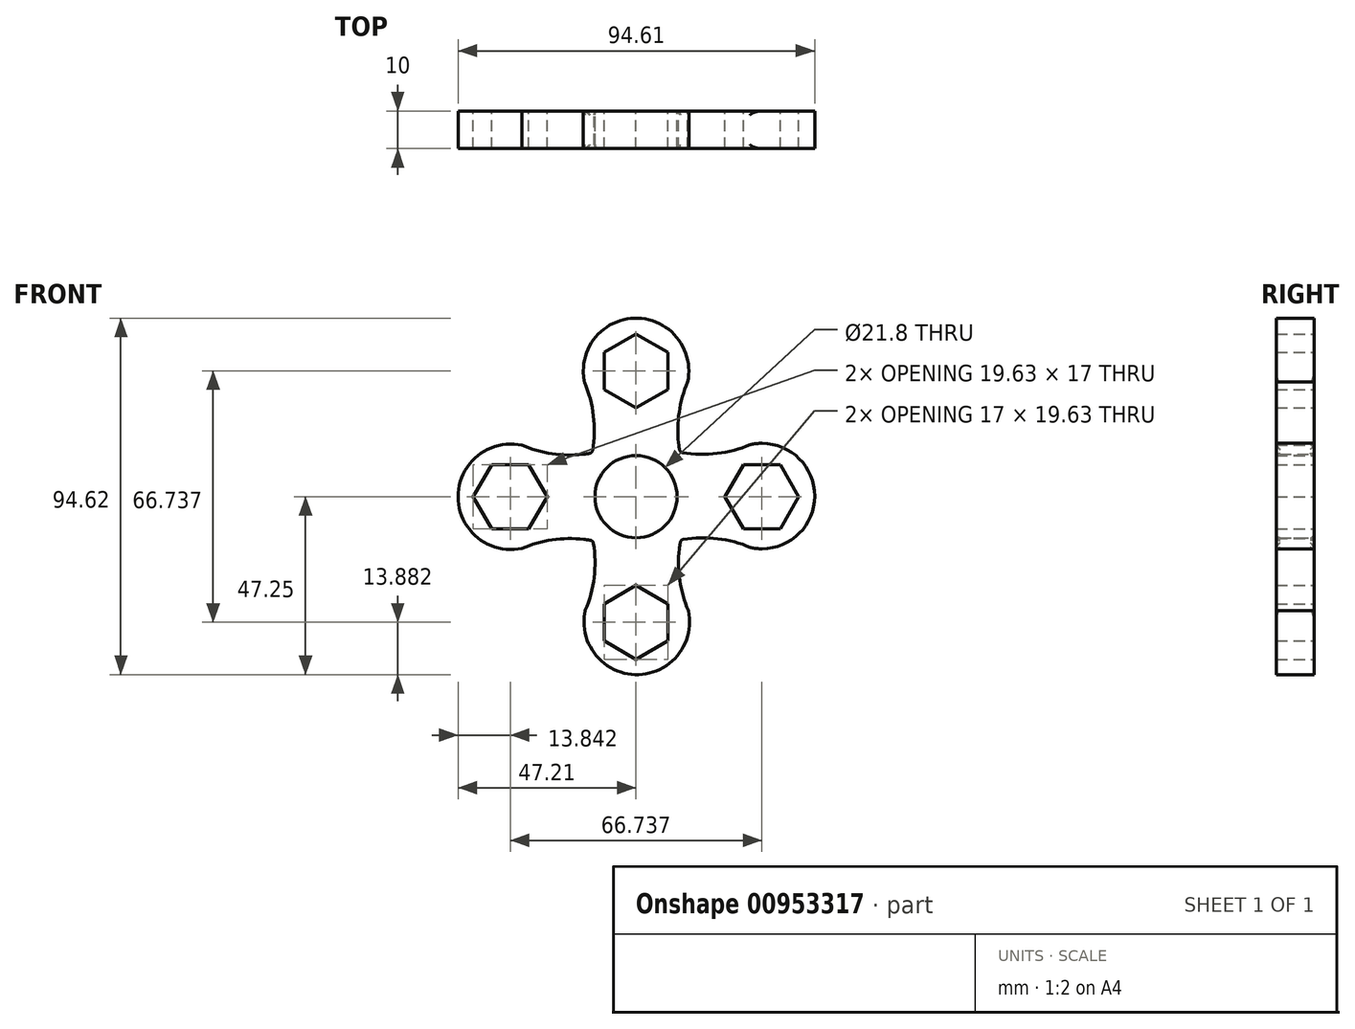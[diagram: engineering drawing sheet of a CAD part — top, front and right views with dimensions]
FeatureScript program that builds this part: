
annotation { "Feature Type Name" : "Feature", "Feature Type Description" : "" }
export const myFeature = defineFeature(function(context is Context, id is Id, definition is map)
    precondition{}
    {
        {
            var Q0;
            Q0=qCreatedBy(makeId("Front.planeOp"),FACE);
            var sketch = newSketch(context, id + "F0", { "sketchPlane" : qUnion([Q0])});
            skCircle(sketch, "E0", {"center": v(0, 0) * mm, "radius": 10.9 * mm});
            skCircle(sketch, "E1.cCircle", {"center": v(0, 33.37) * mm, "radius": 8.5 * mm, "construction": true});
            skLineSegment(sketch, "E1.0", {"start": v(8.5, 38.28) * mm, "end": v(8.5, 28.46) * mm});
            skLineSegment(sketch, "E1.1", {"start": v(8.5, 28.46) * mm, "end": v(0, 23.55) * mm});
            skLineSegment(sketch, "E1.2", {"start": v(0, 23.55) * mm, "end": v(-8.5, 28.46) * mm});
            skLineSegment(sketch, "E1.3", {"start": v(-8.5, 28.46) * mm, "end": v(-8.5, 38.28) * mm});
            skLineSegment(sketch, "E1.4", {"start": v(-8.5, 38.28) * mm, "end": v(0, 43.18) * mm});
            skLineSegment(sketch, "E1.5", {"start": v(0, 43.18) * mm, "end": v(8.5, 38.28) * mm});
            skPoint(sketch, "E1.0.midPoint", {"position": v(8.5, 33.37) * mm});
            skCircle(sketch, "E2.1.0", {"center": v(-33.37, 0) * mm, "radius": 8.5 * mm, "construction": true});
            skLineSegment(sketch, "E2.1.1", {"start": v(-38.28, 8.5) * mm, "end": v(-28.46, 8.5) * mm});
            skLineSegment(sketch, "E2.1.2", {"start": v(-23.55, 0) * mm, "end": v(-28.46, -8.5) * mm});
            skPoint(sketch, "E2.1.3", {"position": v(-33.37, 8.5) * mm});
            skLineSegment(sketch, "E2.1.4", {"start": v(-28.46, 8.5) * mm, "end": v(-23.55, 0) * mm});
            skLineSegment(sketch, "E2.1.5", {"start": v(-28.46, -8.5) * mm, "end": v(-38.28, -8.5) * mm});
            skLineSegment(sketch, "E2.1.6", {"start": v(-43.18, 0) * mm, "end": v(-38.28, 8.5) * mm});
            skLineSegment(sketch, "E2.1.7", {"start": v(-38.28, -8.5) * mm, "end": v(-43.18, 0) * mm});
            skCircle(sketch, "E2.2.0", {"center": v(0, -33.37) * mm, "radius": 8.5 * mm, "construction": true});
            skLineSegment(sketch, "E2.2.1", {"start": v(-8.5, -38.28) * mm, "end": v(-8.5, -28.46) * mm});
            skLineSegment(sketch, "E2.2.2", {"start": v(0, -23.55) * mm, "end": v(8.5, -28.46) * mm});
            skPoint(sketch, "E2.2.3", {"position": v(-8.5, -33.37) * mm});
            skLineSegment(sketch, "E2.2.4", {"start": v(-8.5, -28.46) * mm, "end": v(0, -23.55) * mm});
            skLineSegment(sketch, "E2.2.5", {"start": v(8.5, -28.46) * mm, "end": v(8.5, -38.28) * mm});
            skLineSegment(sketch, "E2.2.6", {"start": v(0, -43.18) * mm, "end": v(-8.5, -38.28) * mm});
            skLineSegment(sketch, "E2.2.7", {"start": v(8.5, -38.28) * mm, "end": v(0, -43.18) * mm});
            skCircle(sketch, "E2.3.0", {"center": v(33.37, 0) * mm, "radius": 8.5 * mm, "construction": true});
            skLineSegment(sketch, "E2.3.1", {"start": v(38.28, -8.5) * mm, "end": v(28.46, -8.5) * mm});
            skLineSegment(sketch, "E2.3.2", {"start": v(23.55, 0) * mm, "end": v(28.46, 8.5) * mm});
            skPoint(sketch, "E2.3.3", {"position": v(33.37, -8.5) * mm});
            skLineSegment(sketch, "E2.3.4", {"start": v(28.46, -8.5) * mm, "end": v(23.55, 0) * mm});
            skLineSegment(sketch, "E2.3.5", {"start": v(28.46, 8.5) * mm, "end": v(38.28, 8.5) * mm});
            skLineSegment(sketch, "E2.3.6", {"start": v(43.18, 0) * mm, "end": v(38.28, -8.5) * mm});
            skLineSegment(sketch, "E2.3.7", {"start": v(38.28, 8.5) * mm, "end": v(43.18, 0) * mm});
            skArc(sketch, "E3", {"start": v(13.68, 30.4) * mm, "mid": v(0, 47.37) * mm, "end": v(-13.68, 30.4) * mm});
            skArc(sketch, "E4", {"start": v(13.68, 30.4) * mm, "mid": v(11.28, 21.26) * mm, "end": v(11.63, 11.82) * mm});
            skArc(sketch, "E5.MirrorCS", {"start": v(-13.68, 30.4) * mm, "mid": v(-11.27, 21.15) * mm, "end": v(-11.67, 11.59) * mm});
            skArc(sketch, "E6.1.0", {"start": v(-30.25, 13.64) * mm, "mid": v(-21.11, 11.25) * mm, "end": v(-11.67, 11.59) * mm});
            skArc(sketch, "E6.1.1", {"start": v(-30.25, -13.72) * mm, "mid": v(-21, -11.3) * mm, "end": v(-11.44, -11.7) * mm});
            skArc(sketch, "E6.1.2", {"start": v(-30.25, 13.64) * mm, "mid": v(-47.21, -0.04) * mm, "end": v(-30.25, -13.72) * mm});
            skArc(sketch, "E6.2.0", {"start": v(-13.5, -30.29) * mm, "mid": v(-11.1, -21.15) * mm, "end": v(-11.44, -11.7) * mm});
            skArc(sketch, "E6.2.1", {"start": v(13.87, -30.29) * mm, "mid": v(11.46, -21.03) * mm, "end": v(11.86, -11.48) * mm});
            skArc(sketch, "E6.2.2", {"start": v(-13.5, -30.29) * mm, "mid": v(0.19, -47.25) * mm, "end": v(13.87, -30.29) * mm});
            skArc(sketch, "E6.3.0", {"start": v(30.44, -13.53) * mm, "mid": v(21.3, -11.13) * mm, "end": v(11.86, -11.48) * mm});
            skArc(sketch, "E6.3.1", {"start": v(30.44, 13.83) * mm, "mid": v(21.18, 11.42) * mm, "end": v(11.63, 11.82) * mm});
            skArc(sketch, "E6.3.2", {"start": v(30.44, -13.53) * mm, "mid": v(47.4, 0.15) * mm, "end": v(30.44, 13.83) * mm});
            skPoint(sketch, "E6.center", {"position": v(0.1, 0.06) * mm});
            skSolve(sketch);
        }
        {
            var Q0;
            Q0 = qSketchRegion(id + "F0", true);
            extrude(context, id + "F1", {"entities" : qUnion([Q0]), "depth" : 10 * mm, "offsetDistance" : 25 * mm});
        }
        {
            var Q0;
            Q0=makeQuery(id+"F1.opExtrude","SWEPT_FACE",FACE,{"disambiguationData":[OSD([sQuery(id+"F0.wireOp",EDGE,"E6.3.1")])]});
            fillet(context, id + "F2", {"entities" : qUnion([Q0]), "radius" : 1 * mm, "tangentPropagation" : true, "allowEdgeOverflow" : false});
        }
        {
            var Q0;
            Q0=makeQuery(id+"F1.opExtrude","SWEPT_FACE",FACE,{"disambiguationData":[OSD([sQuery(id+"F0.wireOp",EDGE,"E6.2.0")])]});
            var Q1;
            Q1=makeQuery(id+"F1.opExtrude","SWEPT_FACE",FACE,{"disambiguationData":[OSD([sQuery(id+"F0.wireOp",EDGE,"E6.3.0")])]});
            var Q2;
            Q2=makeQuery(id+"F1.opExtrude","SWEPT_FACE",FACE,{"disambiguationData":[OSD([sQuery(id+"F0.wireOp",EDGE,"E5.MirrorCS")])]});
            fillet(context, id + "F3", {"entities" : qUnion([Q0, Q1, Q2]), "radius" : 1 * mm, "tangentPropagation" : true, "allowEdgeOverflow" : false});
        }
    });
